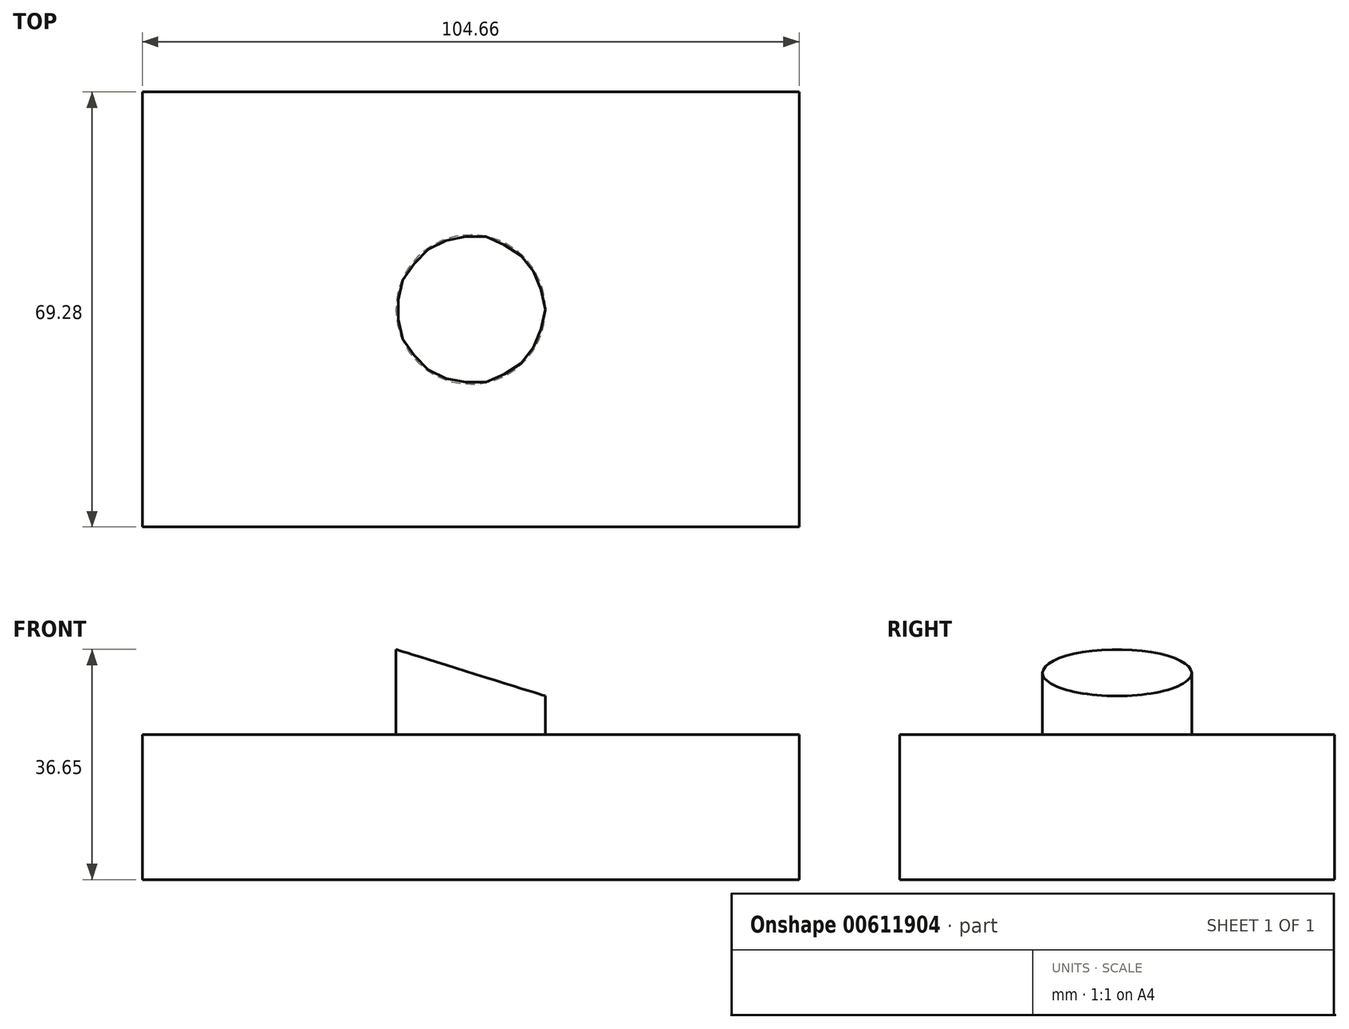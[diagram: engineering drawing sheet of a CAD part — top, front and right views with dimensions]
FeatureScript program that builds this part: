
annotation { "Feature Type Name" : "Feature", "Feature Type Description" : "" }
export const myFeature = defineFeature(function(context is Context, id is Id, definition is map)
    precondition{}
    {
        {
            var Q0;
            Q0=qCreatedBy(makeId("Top.planeOp"),FACE);
            var sketch = newSketch(context, id + "F0", { "sketchPlane" : qUnion([Q0])});
            skLineSegment(sketch, "E0.bottom", {"start": v(52.33, -34.64) * mm, "end": v(-52.33, -34.64) * mm});
            skLineSegment(sketch, "E0.top", {"start": v(52.33, 34.64) * mm, "end": v(-52.33, 34.64) * mm});
            skLineSegment(sketch, "E0.left", {"start": v(52.33, -34.64) * mm, "end": v(52.33, 34.64) * mm});
            skLineSegment(sketch, "E0.right", {"start": v(-52.33, -34.64) * mm, "end": v(-52.33, 34.64) * mm});
            skPoint(sketch, "E0.middle", {"position": v(0, 0) * mm});
            skSolve(sketch);
        }
        {
            var Q0;
            Q0=makeQuery(id+"F0.imprint","IMPRINT",FACE,{"disambiguationData":[TD([[makeQuery(id+"F0.imprint","IMPRINT",EDGE,{"derivedFrom":sQuery(id+"F0.wireOp",EDGE,"E0.bottom")}),-1.0]])]});
            extrude(context, id + "F1", {"entities" : qUnion([Q0]), "depth" : 23.1 * mm, "offsetDistance" : 25.4 * mm});
        }
        {
            var Q0;
            Q0=makeQuery(id+"F1.opExtrude","CAP_FACE",FACE,{"disambiguationData":[OSD([sQuery(id+"F0.wireOp",EDGE,"E0.bottom"),sQuery(id+"F0.wireOp",EDGE,"E0.top"),sQuery(id+"F0.wireOp",EDGE,"E0.left"),sQuery(id+"F0.wireOp",EDGE,"E0.right")])],"isStart":false});
            var sketch = newSketch(context, id + "F2", { "sketchPlane" : qUnion([Q0])});
            skCircle(sketch, "E1", {"center": v(0, 0) * mm, "radius": 11.9 * mm});
            skSolve(sketch);
        }
        {
            var Q0;
            Q0=makeQuery(id+"F2.imprint","IMPRINT",FACE,{"disambiguationData":[TD([[makeQuery(id+"F2.imprint","IMPRINT",EDGE,{"derivedFrom":sQuery(id+"F2.wireOp",EDGE,"E1")}),1.0]])]});
            extrude(context, id + "F3", {"entities" : qUnion([Q0]), "operationType" : NewBodyOperationType.ADD, "depth" : 18.03 * mm, "offsetDistance" : 25.4 * mm});
        }
        {
            var Q0;
            Q0=qCreatedBy(makeId("Front.planeOp"),FACE);
            var sketch = newSketch(context, id + "F4", { "sketchPlane" : qUnion([Q0])});
            skLineSegment(sketch, "E2", {"start": v(-27.22, 41.43) * mm, "end": v(20.99, 26.4) * mm});
            skLineSegment(sketch, "E3", {"start": v(20.99, 26.4) * mm, "end": v(20.99, 43.44) * mm});
            skLineSegment(sketch, "E4", {"start": v(20.99, 43.44) * mm, "end": v(-27.22, 41.43) * mm});
            skSolve(sketch);
        }
        {
            var Q0;
            Q0 = qSketchRegion(id + "F4", true);
            extrude(context, id + "F5", {"entities" : qUnion([Q0]), "operationType" : NewBodyOperationType.REMOVE, "oppositeDirection" : true, "depth" : 25.4 * mm, "offsetDistance" : 25.4 * mm});
        }
        {
            var Q0;
            Q0 = qSketchRegion(id + "F4", true);
            extrude(context, id + "F6", {"entities" : qUnion([Q0]), "operationType" : NewBodyOperationType.REMOVE, "oppositeDirection" : true, "depth" : -25.4 * mm, "offsetDistance" : 25.4 * mm});
        }
    });
